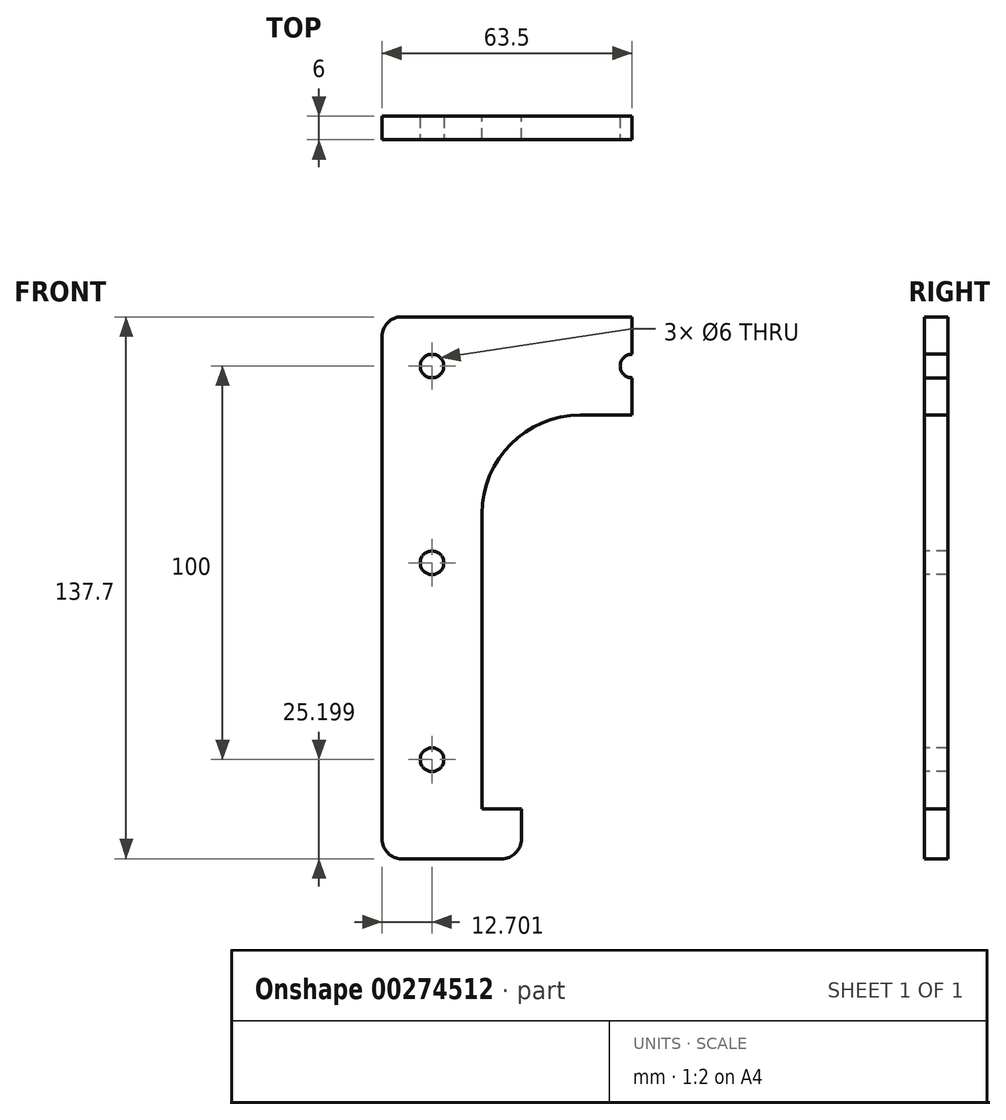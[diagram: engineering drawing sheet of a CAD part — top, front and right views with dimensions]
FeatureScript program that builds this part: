
annotation { "Feature Type Name" : "Feature", "Feature Type Description" : "" }
export const myFeature = defineFeature(function(context is Context, id is Id, definition is map)
    precondition{}
    {
        {
            var Q0;
            Q0=qCreatedBy(makeId("Front.planeOp"),FACE);
            var sketch = newSketch(context, id + "F0", { "sketchPlane" : qUnion([Q0])});
            skLineSegment(sketch, "E0.bottom", {"start": v(-82.96, 33.19) * mm, "end": v(34.04, 33.19) * mm});
            skLineSegment(sketch, "E0.top", {"start": v(-82.96, -104.51) * mm, "end": v(-57.56, -104.51) * mm});
            skLineSegment(sketch, "E0.left", {"start": v(-87.96, 28.19) * mm, "end": v(-87.96, -99.51) * mm});
            skLineSegment(sketch, "E0.right", {"start": v(39.04, 28.19) * mm, "end": v(39.04, -99.51) * mm});
            skLineSegment(sketch, "E1.bottom", {"start": v(-62.56, -91.81) * mm, "end": v(-52.56, -91.81) * mm});
            skLineSegment(sketch, "E1.top", {"start": v(-37.56, 8.19) * mm, "end": v(-11.36, 8.19) * mm});
            skLineSegment(sketch, "E1.left", {"start": v(-62.56, -91.81) * mm, "end": v(-62.56, -16.81) * mm});
            skLineSegment(sketch, "E1.right", {"start": v(13.64, -91.81) * mm, "end": v(13.64, -16.81) * mm});
            skLineSegment(sketch, "E2.left", {"start": v(-52.56, -91.81) * mm, "end": v(-52.56, -99.51) * mm});
            skLineSegment(sketch, "E2.right", {"start": v(3.64, -91.81) * mm, "end": v(3.64, -99.51) * mm});
            skLineSegment(sketch, "E3.trimOffspring", {"start": v(3.64, -91.81) * mm, "end": v(13.64, -91.81) * mm});
            skLineSegment(sketch, "E4.trimOffspring", {"start": v(8.64, -104.51) * mm, "end": v(34.04, -104.51) * mm});
            skPoint(sketch, "E5.visualSharp", {"position": v(-52.56, -104.51) * mm});
            skArc(sketch, "E5.filletArc", {"start": v(-57.56, -104.51) * mm, "mid": v(-54.02, -103.05) * mm, "end": v(-52.56, -99.51) * mm});
            skPoint(sketch, "E6.visualSharp", {"position": v(-87.96, -104.51) * mm});
            skArc(sketch, "E6.filletArc", {"start": v(-87.96, -99.51) * mm, "mid": v(-86.5, -103.05) * mm, "end": v(-82.96, -104.51) * mm});
            skPoint(sketch, "E7.visualSharp", {"position": v(3.64, -104.51) * mm});
            skArc(sketch, "E7.filletArc", {"start": v(3.64, -99.51) * mm, "mid": v(5.1, -103.05) * mm, "end": v(8.64, -104.51) * mm});
            skPoint(sketch, "E8.visualSharp", {"position": v(39.04, -104.51) * mm});
            skArc(sketch, "E8.filletArc", {"start": v(34.04, -104.51) * mm, "mid": v(37.58, -103.05) * mm, "end": v(39.04, -99.51) * mm});
            skPoint(sketch, "E9.visualSharp", {"position": v(39.04, 33.19) * mm});
            skArc(sketch, "E9.filletArc", {"start": v(39.04, 28.19) * mm, "mid": v(37.58, 31.72) * mm, "end": v(34.04, 33.19) * mm});
            skPoint(sketch, "E10.visualSharp", {"position": v(-87.96, 33.19) * mm});
            skArc(sketch, "E10.filletArc", {"start": v(-82.96, 33.19) * mm, "mid": v(-86.5, 31.72) * mm, "end": v(-87.96, 28.19) * mm});
            skPoint(sketch, "E11.visualSharp", {"position": v(-62.56, 8.19) * mm});
            skArc(sketch, "E11.filletArc", {"start": v(-37.56, 8.19) * mm, "mid": v(-55.24, 0.87) * mm, "end": v(-62.56, -16.81) * mm});
            skPoint(sketch, "E12.visualSharp", {"position": v(13.64, 8.19) * mm});
            skArc(sketch, "E12.filletArc", {"start": v(13.64, -16.81) * mm, "mid": v(6.32, 0.87) * mm, "end": v(-11.36, 8.19) * mm});
            skSolve(sketch);
        }
        {
            var Q0;
            Q0 = qSketchRegion(id + "F0", true);
            extrude(context, id + "F1", {"entities" : qUnion([Q0]), "depth" : 6 * mm});
        }
        {
            var Q0;
            Q0=makeQuery(id+"F1.opExtrude","CAP_FACE",FACE,{"disambiguationData":[OSD([sQuery(id+"F0.wireOp",EDGE,"E0.bottom"),sQuery(id+"F0.wireOp",EDGE,"E0.top"),sQuery(id+"F0.wireOp",EDGE,"E0.left"),sQuery(id+"F0.wireOp",EDGE,"E0.right"),sQuery(id+"F0.wireOp",EDGE,"E1.bottom"),sQuery(id+"F0.wireOp",EDGE,"E1.top"),sQuery(id+"F0.wireOp",EDGE,"E1.left"),sQuery(id+"F0.wireOp",EDGE,"E1.right"),sQuery(id+"F0.wireOp",EDGE,"E2.left"),sQuery(id+"F0.wireOp",EDGE,"E2.right"),sQuery(id+"F0.wireOp",EDGE,"E3.trimOffspring"),sQuery(id+"F0.wireOp",EDGE,"E4.trimOffspring"),sQuery(id+"F0.wireOp",EDGE,"E5.filletArc"),sQuery(id+"F0.wireOp",EDGE,"E6.filletArc"),sQuery(id+"F0.wireOp",EDGE,"E7.filletArc"),sQuery(id+"F0.wireOp",EDGE,"E8.filletArc"),sQuery(id+"F0.wireOp",EDGE,"E9.filletArc"),sQuery(id+"F0.wireOp",EDGE,"E10.filletArc"),sQuery(id+"F0.wireOp",EDGE,"E11.filletArc"),sQuery(id+"F0.wireOp",EDGE,"E12.filletArc")])],"isStart":false});
            var sketch = newSketch(context, id + "F2", { "sketchPlane" : qUnion([Q0])});
            skPoint(sketch, "E13", {"position": v(-75.26, 20.69) * mm});
            skPoint(sketch, "E14", {"position": v(-75.26, -29.31) * mm});
            skPoint(sketch, "E15", {"position": v(-75.26, -79.31) * mm});
            skPoint(sketch, "E16", {"position": v(26.34, -79.31) * mm});
            skPoint(sketch, "E17", {"position": v(26.34, -29.31) * mm});
            skPoint(sketch, "E18", {"position": v(26.34, 20.69) * mm});
            skPoint(sketch, "E19", {"position": v(-24.46, 20.69) * mm});
            skSolve(sketch);
        }
        {
            var Q0;
            Q0=sQuery(id+"F2.wireOp",VERTEX,"E13");
            var Q1;
            Q1=sQuery(id+"F2.wireOp",VERTEX,"E14");
            var Q2;
            Q2=sQuery(id+"F2.wireOp",VERTEX,"E15");
            var Q3;
            Q3=sQuery(id+"F2.wireOp",VERTEX,"E19");
            var Q4;
            Q4=sQuery(id+"F2.wireOp",VERTEX,"E18");
            var Q5;
            Q5=sQuery(id+"F2.wireOp",VERTEX,"E17");
            var Q6;
            Q6=sQuery(id+"F2.wireOp",VERTEX,"E16");
            var Q7;
            Q7=makeQuery(id+"F1.opExtrude","SWEPT_BODY",BODY,{"disambiguationData":[OSD([sQuery(id+"F0.wireOp",EDGE,"E0.bottom"),sQuery(id+"F0.wireOp",EDGE,"E0.top"),sQuery(id+"F0.wireOp",EDGE,"E0.left"),sQuery(id+"F0.wireOp",EDGE,"E0.right"),sQuery(id+"F0.wireOp",EDGE,"E1.bottom"),sQuery(id+"F0.wireOp",EDGE,"E1.top"),sQuery(id+"F0.wireOp",EDGE,"E1.left"),sQuery(id+"F0.wireOp",EDGE,"E1.right"),sQuery(id+"F0.wireOp",EDGE,"E2.left"),sQuery(id+"F0.wireOp",EDGE,"E2.right"),sQuery(id+"F0.wireOp",EDGE,"E3.trimOffspring"),sQuery(id+"F0.wireOp",EDGE,"E4.trimOffspring"),sQuery(id+"F0.wireOp",EDGE,"E5.filletArc"),sQuery(id+"F0.wireOp",EDGE,"E6.filletArc"),sQuery(id+"F0.wireOp",EDGE,"E7.filletArc"),sQuery(id+"F0.wireOp",EDGE,"E8.filletArc"),sQuery(id+"F0.wireOp",EDGE,"E9.filletArc"),sQuery(id+"F0.wireOp",EDGE,"E10.filletArc"),sQuery(id+"F0.wireOp",EDGE,"E11.filletArc"),sQuery(id+"F0.wireOp",EDGE,"E12.filletArc")])]});
            hole(context, id + "F3", {"style" : HoleStyle.SIMPLE, "endStyle" : HoleEndStyle.THROUGH, "standardTappedOrClearance" : lookupTablePath({ "standard" : "ISO", "size" : "6", "type" : "Drilled" }), "standardBlindInLast" : lookupTablePath({ "standard" : "ISO", "size" : "6", "type" : "Drilled" }), "holeDiameter" : 6 * mm, "tappedDepth" : 12 * mm, "tapClearance" : 3, "locations" : qUnion([Q0, Q1, Q2, Q3, Q4, Q5, Q6]), "scope" : qUnion([Q7])});
        }
        {
            var Q0;
            Q0=makeQuery(id+"F1.opExtrude","CAP_FACE",FACE,{"disambiguationData":[OSD([sQuery(id+"F0.wireOp",EDGE,"E0.bottom"),sQuery(id+"F0.wireOp",EDGE,"E0.top"),sQuery(id+"F0.wireOp",EDGE,"E0.left"),sQuery(id+"F0.wireOp",EDGE,"E0.right"),sQuery(id+"F0.wireOp",EDGE,"E1.bottom"),sQuery(id+"F0.wireOp",EDGE,"E1.top"),sQuery(id+"F0.wireOp",EDGE,"E1.left"),sQuery(id+"F0.wireOp",EDGE,"E1.right"),sQuery(id+"F0.wireOp",EDGE,"E2.left"),sQuery(id+"F0.wireOp",EDGE,"E2.right"),sQuery(id+"F0.wireOp",EDGE,"E3.trimOffspring"),sQuery(id+"F0.wireOp",EDGE,"E4.trimOffspring"),sQuery(id+"F0.wireOp",EDGE,"E5.filletArc"),sQuery(id+"F0.wireOp",EDGE,"E6.filletArc"),sQuery(id+"F0.wireOp",EDGE,"E7.filletArc"),sQuery(id+"F0.wireOp",EDGE,"E8.filletArc"),sQuery(id+"F0.wireOp",EDGE,"E9.filletArc"),sQuery(id+"F0.wireOp",EDGE,"E10.filletArc"),sQuery(id+"F0.wireOp",EDGE,"E11.filletArc"),sQuery(id+"F0.wireOp",EDGE,"E12.filletArc")])],"isStart":false});
            var sketch = newSketch(context, id + "F4", { "sketchPlane" : qUnion([Q0])});
            skLineSegment(sketch, "E20.bottom", {"start": v(-24.46, 33.19) * mm, "end": v(39.04, 33.19) * mm});
            skLineSegment(sketch, "E20.top", {"start": v(-24.46, -106.81) * mm, "end": v(39.04, -106.81) * mm});
            skLineSegment(sketch, "E20.left", {"start": v(-24.46, 33.19) * mm, "end": v(-24.46, -106.81) * mm});
            skLineSegment(sketch, "E20.right", {"start": v(39.04, 33.19) * mm, "end": v(39.04, -106.81) * mm});
            skSolve(sketch);
        }
        {
            var Q0;
            Q0 = qSketchRegion(id + "F4", true);
            extrude(context, id + "F5", {"entities" : qUnion([Q0]), "operationType" : NewBodyOperationType.REMOVE, "oppositeDirection" : true, "depth" : 25 * mm});
        }
    });
